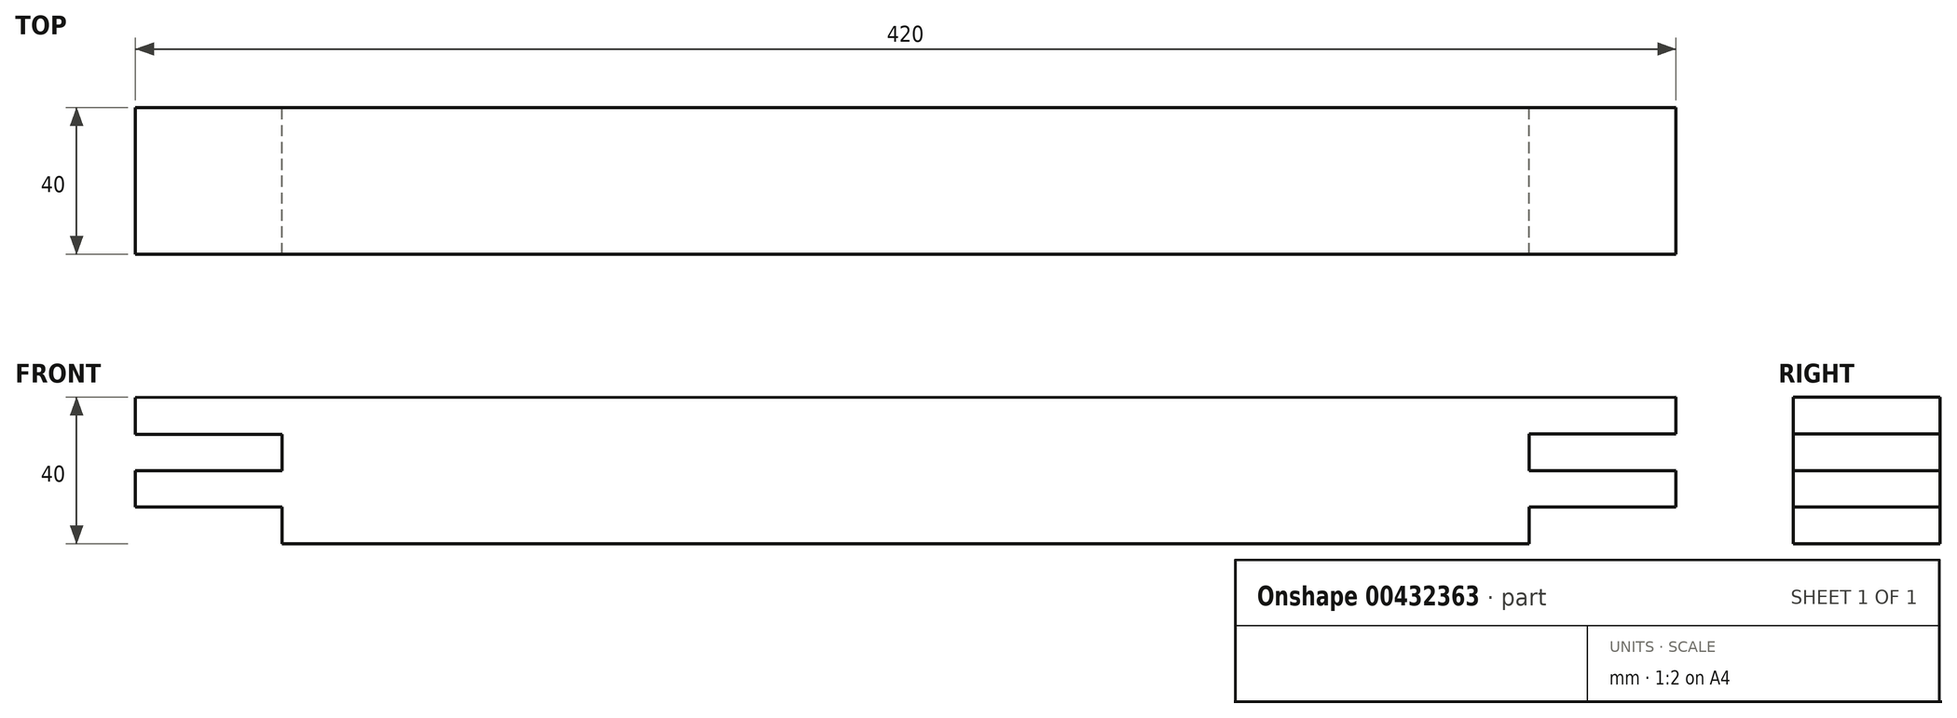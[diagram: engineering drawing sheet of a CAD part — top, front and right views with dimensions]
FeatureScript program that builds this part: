
annotation { "Feature Type Name" : "Feature", "Feature Type Description" : "" }
export const myFeature = defineFeature(function(context is Context, id is Id, definition is map)
    precondition{}
    {
        {
            var Q0;
            Q0=qCreatedBy(makeId("Front.planeOp"),FACE);
            var sketch = newSketch(context, id + "F0", { "sketchPlane" : qUnion([Q0])});
            skLineSegment(sketch, "E0.top", {"start": v(-170, -20) * mm, "end": v(170, -20) * mm});
            skPoint(sketch, "E0.middle", {"position": v(0, 0) * mm});
            skLineSegment(sketch, "E1", {"start": v(-170, -20) * mm, "end": v(-170, -10) * mm});
            skLineSegment(sketch, "E2", {"start": v(-170, -10) * mm, "end": v(-210, -10) * mm});
            skLineSegment(sketch, "E3", {"start": v(-210, -10) * mm, "end": v(-210, 0) * mm});
            skLineSegment(sketch, "E4", {"start": v(-210, 0) * mm, "end": v(-170, 0) * mm});
            skLineSegment(sketch, "E5", {"start": v(-170, 0) * mm, "end": v(-170, 9.9) * mm});
            skLineSegment(sketch, "E6", {"start": v(-170, 9.9) * mm, "end": v(-210, 9.9) * mm});
            skLineSegment(sketch, "E7", {"start": v(-210, 9.9) * mm, "end": v(-210, 19.9) * mm});
            skLineSegment(sketch, "E8", {"start": v(170, -20) * mm, "end": v(170, -10) * mm});
            skLineSegment(sketch, "E9", {"start": v(170, -10) * mm, "end": v(210, -10) * mm});
            skLineSegment(sketch, "E10", {"start": v(210, -10) * mm, "end": v(210, 0) * mm});
            skLineSegment(sketch, "E11", {"start": v(210, 0) * mm, "end": v(170, 0) * mm});
            skLineSegment(sketch, "E12", {"start": v(170, 0) * mm, "end": v(170, 10) * mm});
            skLineSegment(sketch, "E13", {"start": v(170, 10) * mm, "end": v(210, 10) * mm});
            skLineSegment(sketch, "E14", {"start": v(210, 10) * mm, "end": v(210, 20) * mm});
            skLineSegment(sketch, "E15", {"start": v(210, 20) * mm, "end": v(-210, 19.9) * mm});
            skSolve(sketch);
        }
        {
            var Q0;
            Q0 = qSketchRegion(id + "F0", true);
            extrude(context, id + "F1", {"entities" : qUnion([Q0]), "endBound" : BoundingType.SYMMETRIC, "depth" : 40 * mm});
        }
    });
